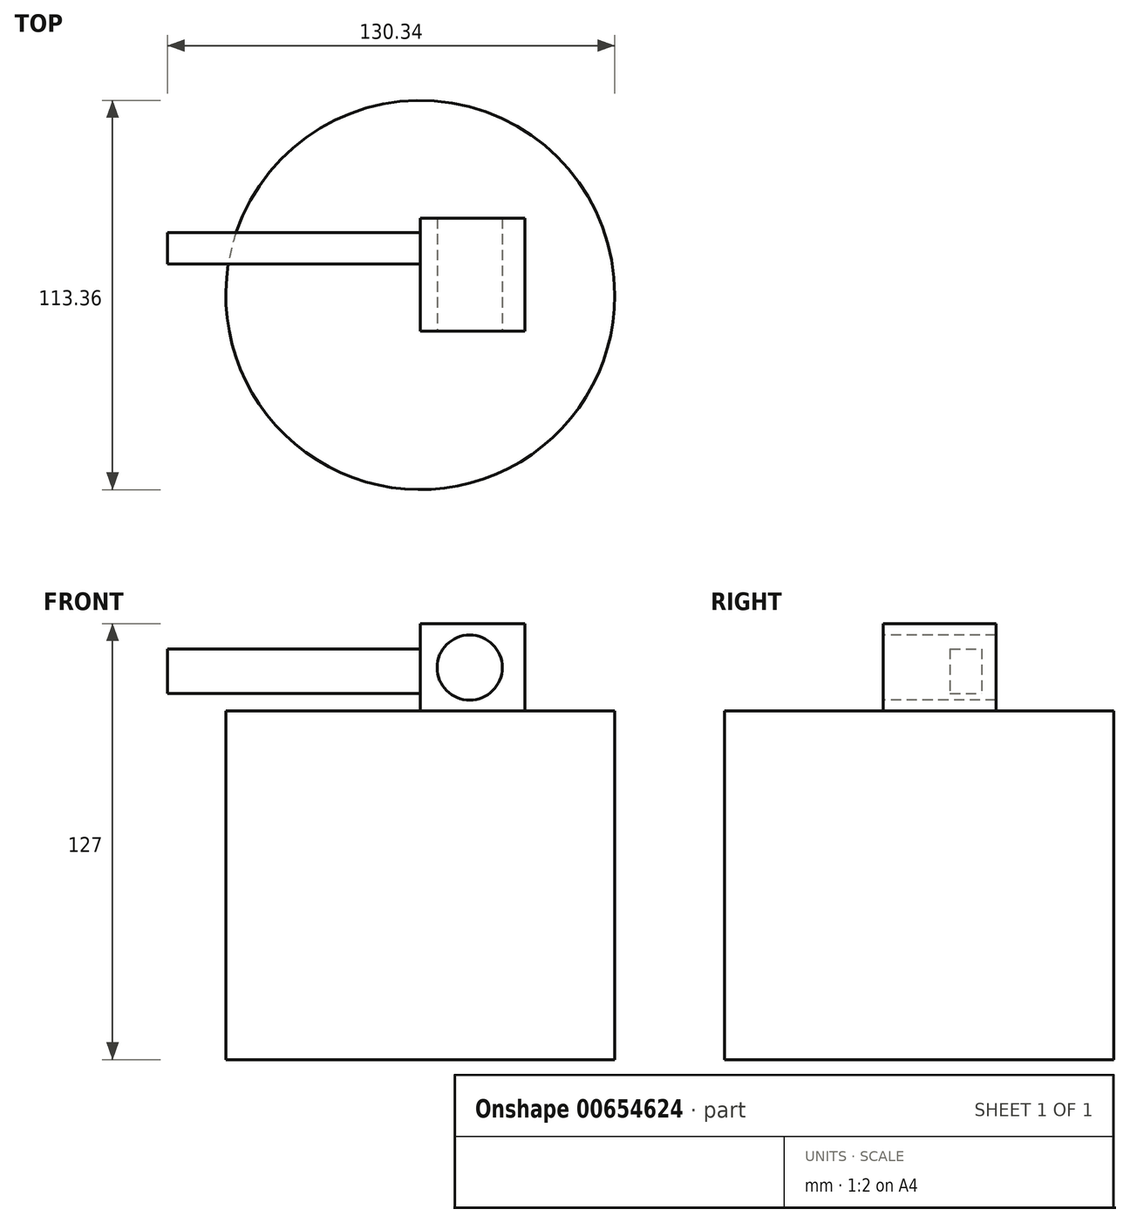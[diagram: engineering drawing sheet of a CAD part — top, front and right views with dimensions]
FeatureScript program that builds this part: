
annotation { "Feature Type Name" : "Feature", "Feature Type Description" : "" }
export const myFeature = defineFeature(function(context is Context, id is Id, definition is map)
    precondition{}
    {
        {
            var Q0;
            Q0=qCreatedBy(makeId("Top.planeOp"),FACE);
            var sketch = newSketch(context, id + "F0", { "sketchPlane" : qUnion([Q0])});
            skCircle(sketch, "E0", {"center": v(0, 0) * mm, "radius": 56.68 * mm});
            skSolve(sketch);
        }
        {
            var Q0;
            Q0 = qSketchRegion(id + "F0", true);
            extrude(context, id + "F1", {"entities" : qUnion([Q0]), "depth" : 101.6 * mm, "offsetDistance" : 25.4 * mm});
        }
        {
            var Q0;
            Q0=makeQuery(id+"F1.opExtrude","CAP_FACE",FACE,{"disambiguationData":[OSD([sQuery(id+"F0.wireOp",EDGE,"E0")])],"isStart":false});
            var sketch = newSketch(context, id + "F2", { "sketchPlane" : qUnion([Q0])});
            skLineSegment(sketch, "E1.bottom", {"start": v(0, 22.35) * mm, "end": v(30.47, 22.35) * mm});
            skLineSegment(sketch, "E1.top", {"start": v(0, -10.46) * mm, "end": v(30.47, -10.46) * mm});
            skLineSegment(sketch, "E1.left", {"start": v(0, 22.35) * mm, "end": v(0, -10.46) * mm});
            skLineSegment(sketch, "E1.right", {"start": v(30.47, 22.35) * mm, "end": v(30.47, -10.46) * mm});
            skSolve(sketch);
        }
        {
            var Q0;
            Q0 = qSketchRegion(id + "F2", true);
            extrude(context, id + "F3", {"entities" : qUnion([Q0]), "operationType" : NewBodyOperationType.ADD, "depth" : 25.4 * mm, "offsetDistance" : 25.4 * mm});
        }
        {
            var Q0;
            Q0=makeQuery(id+"F3.opExtrude","SWEPT_FACE",FACE,{"disambiguationData":[OSD([sQuery(id+"F2.wireOp",EDGE,"E1.left")])]});
            var sketch = newSketch(context, id + "F4", { "sketchPlane" : qUnion([Q0])});
            skLineSegment(sketch, "E2.bottom", {"start": v(-8.98, 119.64) * mm, "end": v(-18.2, 119.64) * mm});
            skLineSegment(sketch, "E2.top", {"start": v(-8.98, 106.64) * mm, "end": v(-18.2, 106.64) * mm});
            skLineSegment(sketch, "E2.left", {"start": v(-8.98, 119.64) * mm, "end": v(-8.98, 106.64) * mm});
            skLineSegment(sketch, "E2.right", {"start": v(-18.2, 119.64) * mm, "end": v(-18.2, 106.64) * mm});
            skSolve(sketch);
        }
        {
            var Q0;
            Q0 = qSketchRegion(id + "F4", true);
            extrude(context, id + "F5", {"entities" : qUnion([Q0]), "operationType" : NewBodyOperationType.ADD, "depth" : 73.66 * mm, "offsetDistance" : 25.4 * mm});
        }
        {
            var Q0;
            Q0=makeQuery(id+"F3.opExtrude","SWEPT_FACE",FACE,{"disambiguationData":[OSD([sQuery(id+"F2.wireOp",EDGE,"E1.top")])]});
            var sketch = newSketch(context, id + "F6", { "sketchPlane" : qUnion([Q0])});
            skCircle(sketch, "E3", {"center": v(14.4, 114.18) * mm, "radius": 9.5 * mm});
            skSolve(sketch);
        }
        {
            var Q0;
            Q0 = qSketchRegion(id + "F6", true);
            extrude(context, id + "F7", {"entities" : qUnion([Q0]), "operationType" : NewBodyOperationType.REMOVE, "oppositeDirection" : true, "depth" : 50.8 * mm, "offsetDistance" : 25.4 * mm});
        }
    });
